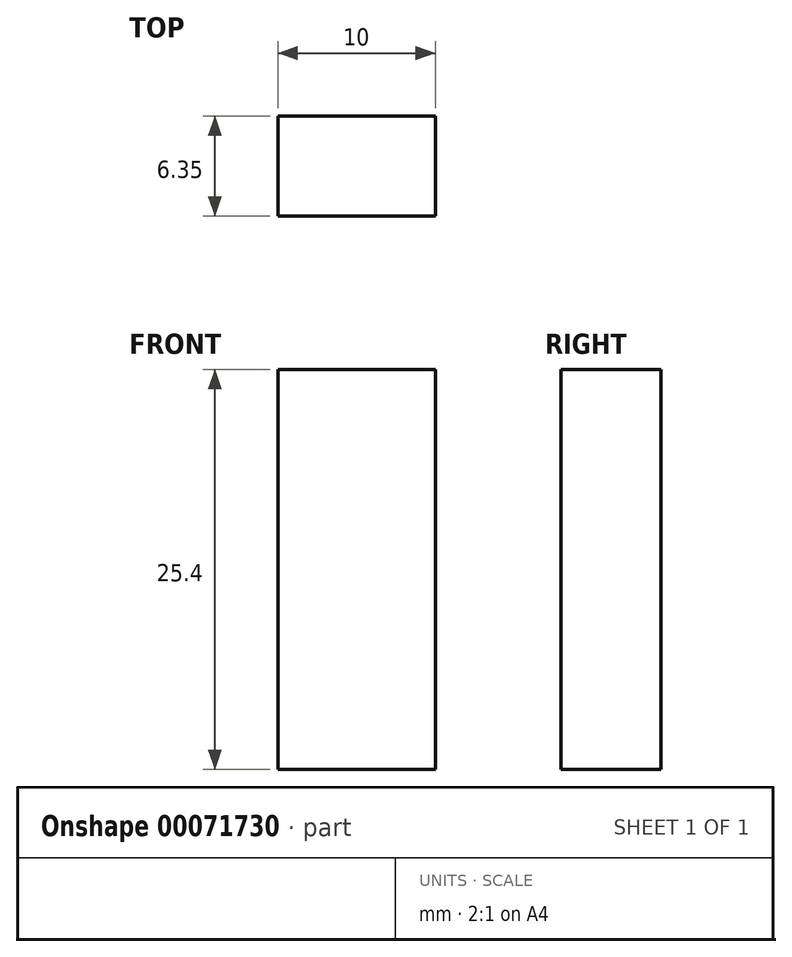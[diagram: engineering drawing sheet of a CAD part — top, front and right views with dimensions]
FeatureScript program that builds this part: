
annotation { "Feature Type Name" : "Feature", "Feature Type Description" : "" }
export const myFeature = defineFeature(function(context is Context, id is Id, definition is map)
    precondition{}
    {
        {
            var Q0;
            Q0=qCreatedBy(makeId("Front.planeOp"),FACE);
            var sketch = newSketch(context, id + "F0", { "sketchPlane" : qUnion([Q0])});
            skLineSegment(sketch, "E0.bottom", {"start": v(0, 12.7) * mm, "end": v(10, 12.7) * mm});
            skLineSegment(sketch, "E0.top", {"start": v(0, -12.7) * mm, "end": v(10, -12.7) * mm});
            skLineSegment(sketch, "E0.left", {"start": v(0, 12.7) * mm, "end": v(0, -12.7) * mm});
            skLineSegment(sketch, "E0.right", {"start": v(10, 12.7) * mm, "end": v(10, -12.7) * mm});
            skSolve(sketch);
        }
        {
            var Q0;
            Q0=makeQuery(id+"F0.imprint","IMPRINT",FACE,{"disambiguationData":[TD([[makeQuery(id+"F0.imprint","IMPRINT",EDGE,{"derivedFrom":sQuery(id+"F0.wireOp",EDGE,"E0.bottom")}),-1.0]])]});
            extrude(context, id + "F1", {"entities" : qUnion([Q0]), "depth" : 6.35 * mm});
        }
    });
